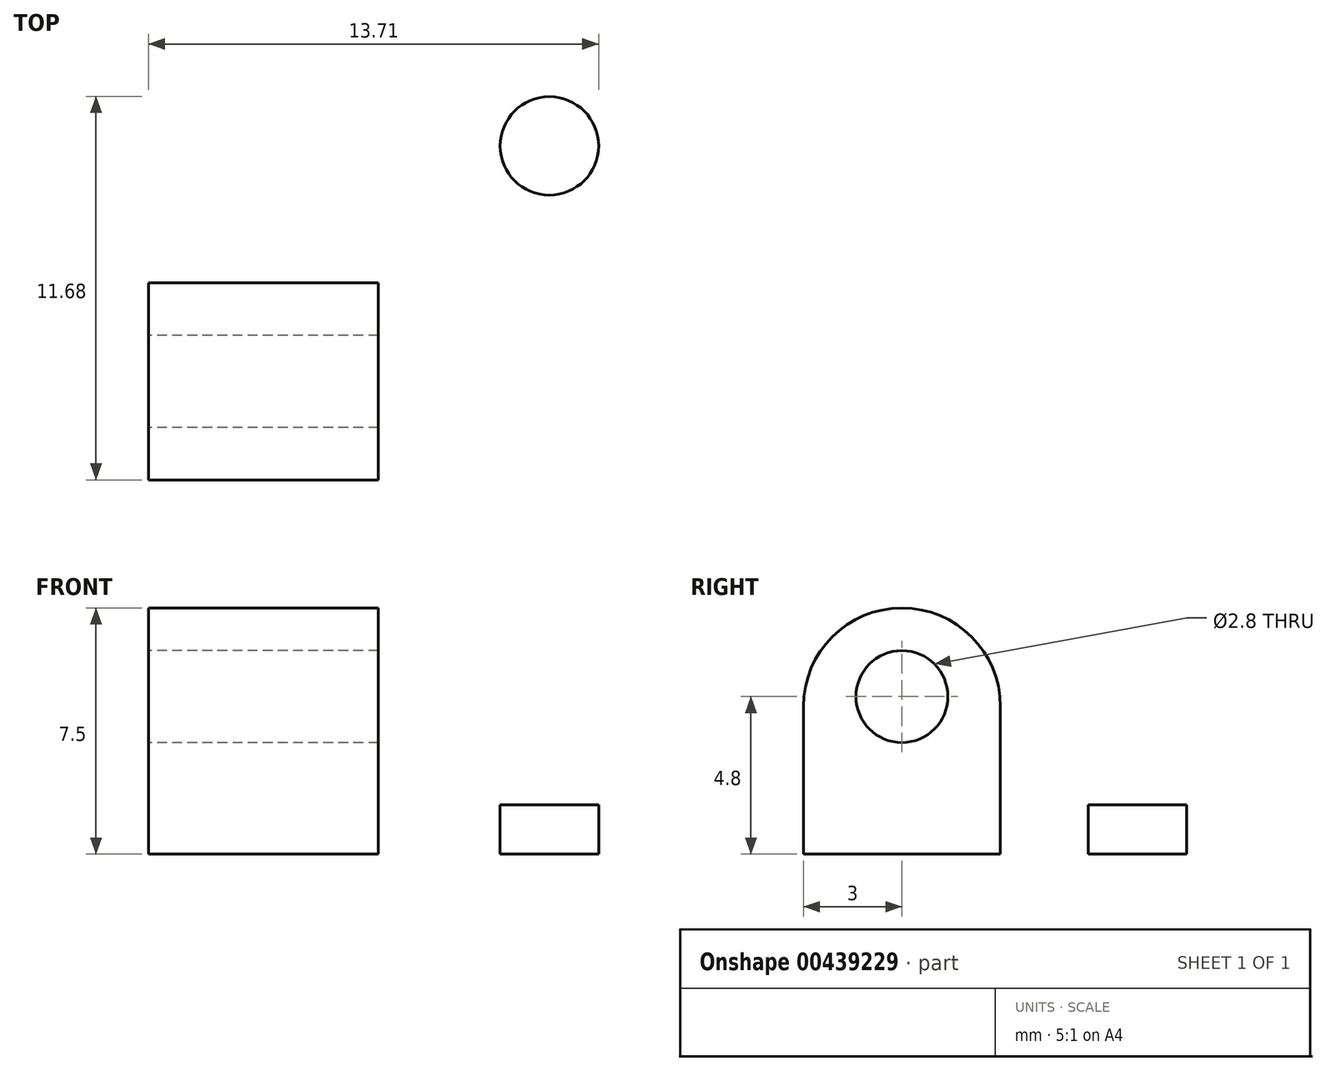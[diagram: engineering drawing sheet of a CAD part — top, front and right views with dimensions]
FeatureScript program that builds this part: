
annotation { "Feature Type Name" : "Feature", "Feature Type Description" : "" }
export const myFeature = defineFeature(function(context is Context, id is Id, definition is map)
    precondition{}
    {
        {
            var Q0;
            Q0=qCreatedBy(makeId("Top.planeOp"),FACE);
            var sketch = newSketch(context, id + "F0", { "sketchPlane" : qUnion([Q0])});
            skPoint(sketch, "E0.middle", {"position": v(0, 0) * mm});
            skCircle(sketch, "E1", {"center": v(-8.71, 7.17) * mm, "radius": 1.5 * mm});
            skCircle(sketch, "E2.MirrorC", {"center": v(8.71, 7.17) * mm, "radius": 1.5 * mm});
            skCircle(sketch, "E3.MirrorC", {"center": v(-8.71, -7.17) * mm, "radius": 1.5 * mm});
            skCircle(sketch, "E4.MirrorC", {"center": v(8.71, -7.17) * mm, "radius": 1.5 * mm});
            skArc(sketch, "E5.0", {"start": v(-5.56, 5.66) * mm, "mid": v(-11.16, 9.67) * mm, "end": v(-7.24, 4) * mm});
            skArc(sketch, "E6.MirrorC", {"start": v(5.56, 5.66) * mm, "mid": v(11.16, 9.67) * mm, "end": v(7.24, 4) * mm});
            skArc(sketch, "E7.MirrorC", {"start": v(-5.56, -5.66) * mm, "mid": v(-11.16, -9.67) * mm, "end": v(-7.24, -4) * mm});
            skArc(sketch, "E8.MirrorC", {"start": v(5.56, -5.66) * mm, "mid": v(11.16, -9.67) * mm, "end": v(7.24, -4) * mm});
            skPoint(sketch, "E9.orphan", {"position": v(8.7, 7.18) * mm});
            skPoint(sketch, "E10.orphan", {"position": v(8.71, -7.18) * mm});
            skPoint(sketch, "E11.trimOffspring.end.orphan", {"position": v(-8.71, -7.18) * mm});
            skFitSpline(sketch, "E12", {"points": [v(-5.56, 5.66) * mm, v(0, 3.17) * mm], "startDerivative": vector(4.38, -6.32) * mm, "endDerivative": vector(9.84, -0.42) * mm});
            skFitSpline(sketch, "E13.MirrorCS", {"points": [v(5.56, 5.66) * mm, v(0, 3.17) * mm], "startDerivative": vector(-4.38, -6.32) * mm, "endDerivative": vector(-9.84, -0.42) * mm});
            skFitSpline(sketch, "E14.MirrorCS", {"points": [v(-5.56, -5.66) * mm, v(0, -3.17) * mm], "startDerivative": vector(4.38, 6.32) * mm, "endDerivative": vector(9.84, 0.42) * mm});
            skFitSpline(sketch, "E15.MirrorCS", {"points": [v(5.56, -5.66) * mm, v(0, -3.17) * mm], "startDerivative": vector(-4.38, 6.32) * mm, "endDerivative": vector(-9.84, 0.42) * mm});
            skFitSpline(sketch, "E16", {"points": [v(-7.24, 4) * mm, v(-5.8, 0) * mm], "startDerivative": vector(3.12, -3.27) * mm, "endDerivative": vector(0.1, -8.92) * mm});
            skFitSpline(sketch, "E17.MirrorCS", {"points": [v(7.24, 4) * mm, v(5.8, 0) * mm], "startDerivative": vector(-3.12, -3.27) * mm, "endDerivative": vector(-0.1, -8.92) * mm});
            skFitSpline(sketch, "E18.MirrorCS", {"points": [v(7.24, -4) * mm, v(5.8, 0) * mm], "startDerivative": vector(-3.12, 3.27) * mm, "endDerivative": vector(-0.1, 8.92) * mm});
            skFitSpline(sketch, "E19.MirrorCS", {"points": [v(-7.24, -4) * mm, v(-5.8, 0) * mm], "startDerivative": vector(3.12, 3.27) * mm, "endDerivative": vector(0.1, 8.92) * mm});
            skLineSegment(sketch, "E20.bottom", {"start": v(3.5, -3) * mm, "end": v(-3.5, -3) * mm});
            skLineSegment(sketch, "E20.top", {"start": v(3.5, 3) * mm, "end": v(-3.5, 3) * mm});
            skLineSegment(sketch, "E20.left", {"start": v(3.5, -3) * mm, "end": v(3.5, 3) * mm});
            skLineSegment(sketch, "E20.right", {"start": v(-3.5, -3) * mm, "end": v(-3.5, 3) * mm});
            skSolve(sketch);
        }
        {
            var Q0;
            Q0=makeQuery(id+"F0.imprint","IMPRINT",FACE,{"disambiguationData":[TD([[makeQuery(id+"F0.imprint","IMPRINT",EDGE,{"derivedFrom":sQuery(id+"F0.wireOp",EDGE,"E2.MirrorC")}),1.0]])]});
            extrude(context, id + "F1", {"entities" : qUnion([Q0]), "depth" : 1.5 * mm, "offsetDistance" : 25 * mm});
        }
        {
            var Q0;
            Q0=makeQuery(id+"F0.imprint","IMPRINT",FACE,{"disambiguationData":[TD([[makeQuery(id+"F0.imprint","IMPRINT",EDGE,{"derivedFrom":sQuery(id+"F0.wireOp",EDGE,"E20.bottom")}),-1.0]])]});
            extrude(context, id + "F2", {"entities" : qUnion([Q0]), "operationType" : NewBodyOperationType.ADD, "depth" : 7.5 * mm, "offsetDistance" : 25 * mm});
        }
        {
            var Q0;
            Q0=makeQuery(id+"F2.opExtrude","SWEPT_FACE",FACE,{"disambiguationData":[OSD([sQuery(id+"F0.wireOp",EDGE,"E20.right")])]});
            var sketch = newSketch(context, id + "F3", { "sketchPlane" : qUnion([Q0])});
            skCircle(sketch, "E21", {"center": v(0, 4.8) * mm, "radius": 1.4 * mm});
            skPoint(sketch, "E21.centerSnap0", {"position": v(0, 7.5) * mm});
            skSolve(sketch);
        }
        {
            var Q0;
            Q0=makeQuery(id+"F3.imprint","IMPRINT",FACE,{"disambiguationData":[TD([[makeQuery(id+"F3.imprint","IMPRINT",EDGE,{"derivedFrom":sQuery(id+"F3.wireOp",EDGE,"E21")}),1.0]])]});
            extrude(context, id + "F4", {"entities" : qUnion([Q0]), "operationType" : NewBodyOperationType.REMOVE, "oppositeDirection" : true, "depth" : 25 * mm, "offsetDistance" : 25 * mm});
        }
        {
            var Q0;
            Q0=makeQuery(id+"F2.opExtrude","CAP_EDGE",EDGE,{"disambiguationData":[OSD([sQuery(id+"F0.wireOp",EDGE,"E20.top")])],"isStart":false});
            var Q1;
            Q1=makeQuery(id+"F2.opExtrude","CAP_EDGE",EDGE,{"disambiguationData":[OSD([sQuery(id+"F0.wireOp",EDGE,"E20.bottom")])],"isStart":false});
            fillet(context, id + "F5", {"entities" : qUnion([Q0, Q1]), "radius" : 3 * mm, "tangentPropagation" : true, "allowEdgeOverflow" : false});
        }
    });
